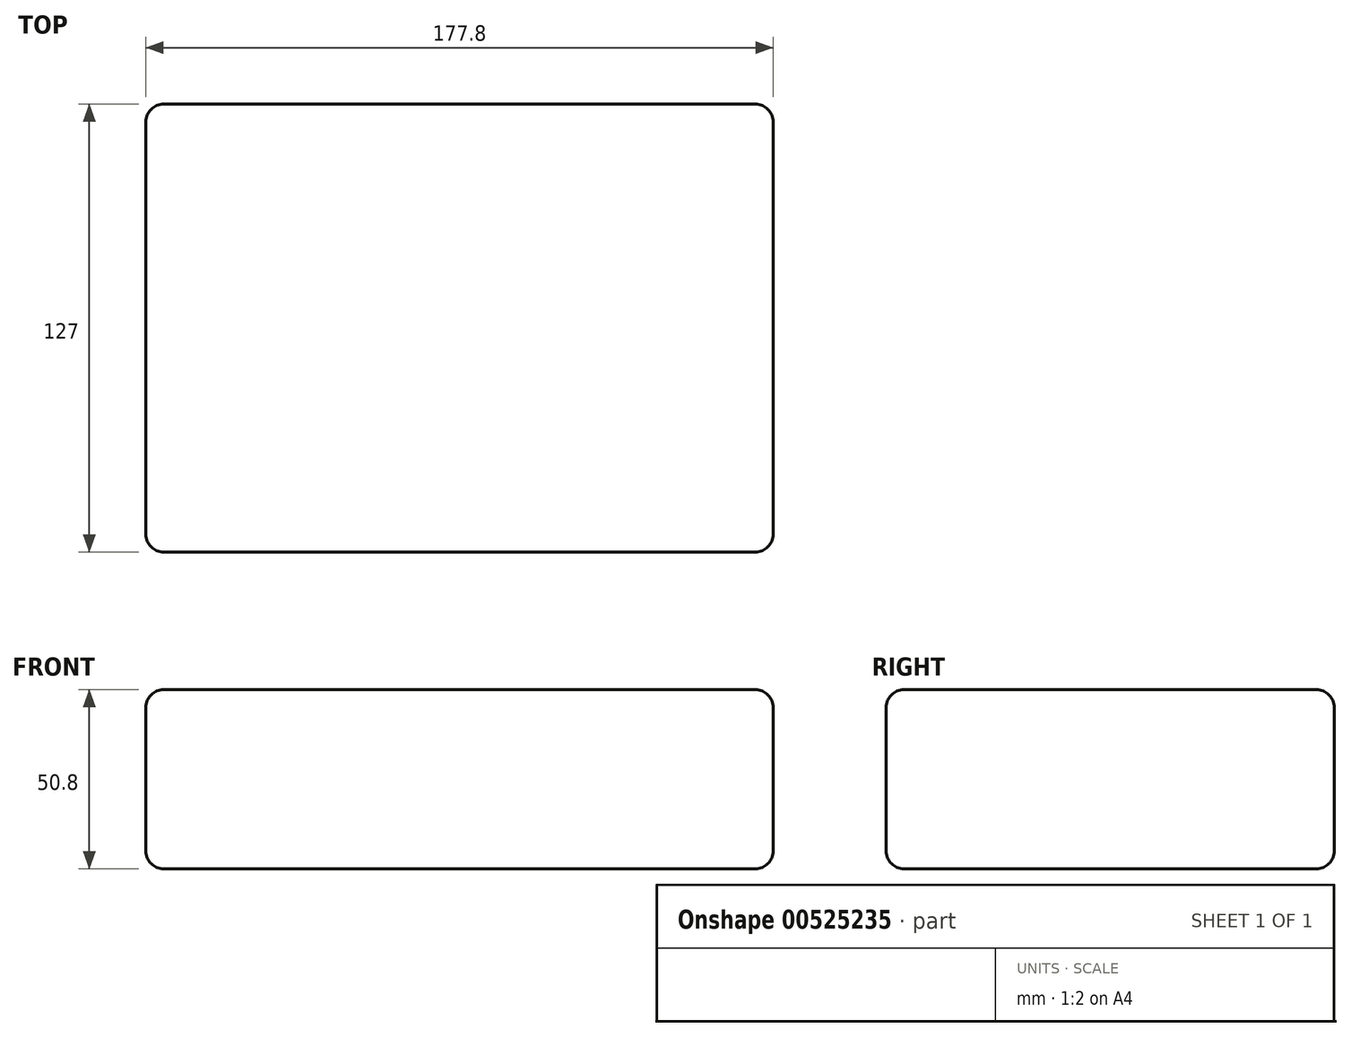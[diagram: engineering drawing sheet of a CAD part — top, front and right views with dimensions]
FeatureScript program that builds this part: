
annotation { "Feature Type Name" : "Feature", "Feature Type Description" : "" }
export const myFeature = defineFeature(function(context is Context, id is Id, definition is map)
    precondition{}
    {
        {
            var Q0;
            Q0=qCreatedBy(makeId("Top.planeOp"),FACE);
            var sketch = newSketch(context, id + "F0", { "sketchPlane" : qUnion([Q0])});
            skLineSegment(sketch, "E0.bottom", {"start": v(-88.9, 63.5) * mm, "end": v(88.9, 63.5) * mm});
            skLineSegment(sketch, "E0.top", {"start": v(-88.9, -63.5) * mm, "end": v(88.9, -63.5) * mm});
            skLineSegment(sketch, "E0.left", {"start": v(-88.9, 63.5) * mm, "end": v(-88.9, -63.5) * mm});
            skLineSegment(sketch, "E0.right", {"start": v(88.9, 63.5) * mm, "end": v(88.9, -63.5) * mm});
            skPoint(sketch, "E0.middle", {"position": v(0, 0) * mm});
            skSolve(sketch);
        }
        {
            var Q0;
            Q0 = qSketchRegion(id + "F0", true);
            extrude(context, id + "F1", {"entities" : qUnion([Q0]), "depth" : 50.8 * mm, "offsetDistance" : 25.4 * mm});
        }
        {
            var Q0;
            Q0=makeQuery(id+"F1.opExtrude","CAP_FACE",FACE,{"disambiguationData":[OSD([sQuery(id+"F0.wireOp",EDGE,"E0.bottom"),sQuery(id+"F0.wireOp",EDGE,"E0.top"),sQuery(id+"F0.wireOp",EDGE,"E0.left"),sQuery(id+"F0.wireOp",EDGE,"E0.right")])],"isStart":false});
            var Q1;
            Q1=makeQuery(id+"F1.opExtrude","SWEPT_FACE",FACE,{"disambiguationData":[OSD([sQuery(id+"F0.wireOp",EDGE,"E0.left")])]});
            var Q2;
            Q2=makeQuery(id+"F1.opExtrude","SWEPT_FACE",FACE,{"disambiguationData":[OSD([sQuery(id+"F0.wireOp",EDGE,"E0.top")])]});
            var Q3;
            Q3=makeQuery(id+"F1.opExtrude","SWEPT_FACE",FACE,{"disambiguationData":[OSD([sQuery(id+"F0.wireOp",EDGE,"E0.right")])]});
            var Q4;
            Q4=makeQuery(id+"F1.opExtrude","CAP_EDGE",EDGE,{"disambiguationData":[OSD([sQuery(id+"F0.wireOp",EDGE,"E0.bottom")])],"isStart":false});
            var Q5;
            Q5=makeQuery(id+"F1.opExtrude","CAP_FACE",FACE,{"disambiguationData":[OSD([sQuery(id+"F0.wireOp",EDGE,"E0.bottom"),sQuery(id+"F0.wireOp",EDGE,"E0.top"),sQuery(id+"F0.wireOp",EDGE,"E0.left"),sQuery(id+"F0.wireOp",EDGE,"E0.right")])],"isStart":true});
            var Q6;
            Q6=makeQuery(id+"F1.opExtrude","CAP_EDGE",EDGE,{"disambiguationData":[OSD([sQuery(id+"F0.wireOp",EDGE,"E0.top")])],"isStart":false});
            var Q7;
            Q7=makeQuery(id+"F1.opExtrude","CAP_EDGE",EDGE,{"disambiguationData":[OSD([sQuery(id+"F0.wireOp",EDGE,"E0.bottom")])],"isStart":true});
            fillet(context, id + "F2", {"entities" : qUnion([Q0, Q1, Q2, Q3, Q4, Q5, Q6, Q7]), "radius" : 5.08 * mm, "tangentPropagation" : true, "allowEdgeOverflow" : false});
        }
    });
